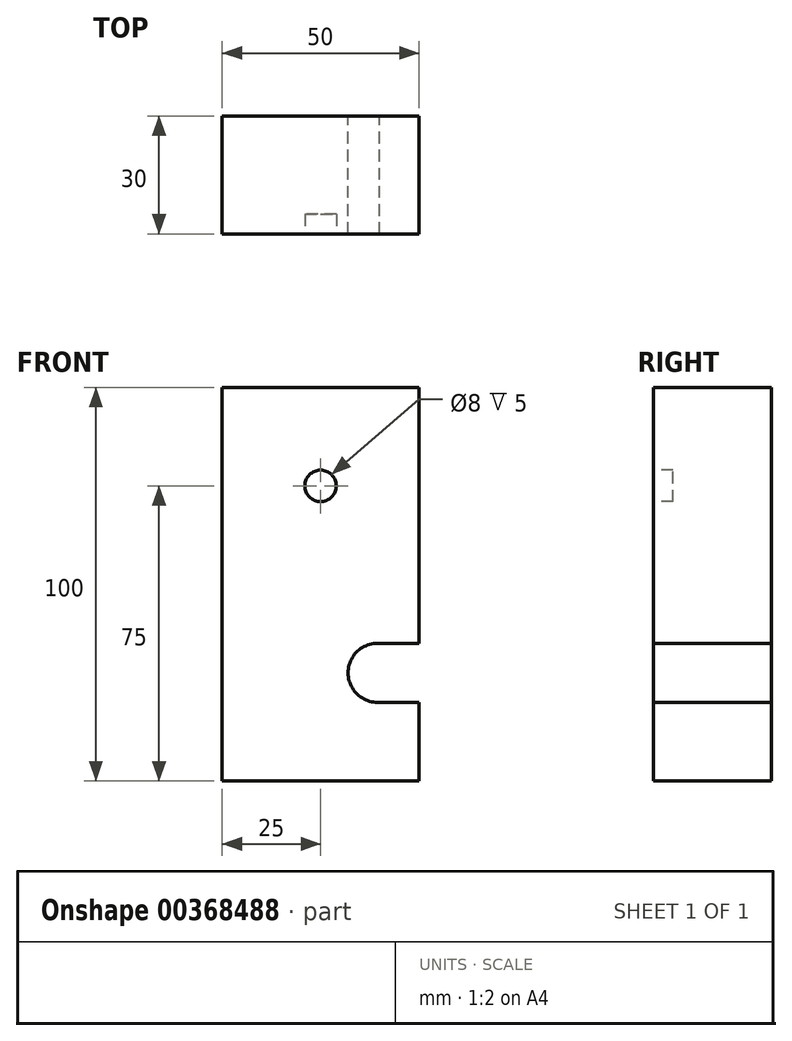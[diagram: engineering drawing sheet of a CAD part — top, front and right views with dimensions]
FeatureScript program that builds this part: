
annotation { "Feature Type Name" : "Feature", "Feature Type Description" : "" }
export const myFeature = defineFeature(function(context is Context, id is Id, definition is map)
    precondition{}
    {
        {
            var Q0;
            Q0=qCreatedBy(makeId("Front.planeOp"),FACE);
            var sketch = newSketch(context, id + "F0", { "sketchPlane" : qUnion([Q0])});
            skLineSegment(sketch, "E0.bottom", {"start": v(-50, 50) * mm, "end": v(0, 50) * mm});
            skLineSegment(sketch, "E0.top", {"start": v(-50, -50) * mm, "end": v(0, -50) * mm});
            skLineSegment(sketch, "E0.left", {"start": v(-50, 50) * mm, "end": v(-50, -50) * mm});
            skPoint(sketch, "E0.middle", {"position": v(0, 0) * mm});
            skLineSegment(sketch, "E1", {"start": v(0, 50) * mm, "end": v(0, -15) * mm});
            skPoint(sketch, "E0.right.start.orphan", {"position": v(50, 50) * mm});
            skPoint(sketch, "E2.orphan", {"position": v(50, -50) * mm});
            skLineSegment(sketch, "E3.bottom", {"start": v(0, -15) * mm, "end": v(-10, -15) * mm});
            skLineSegment(sketch, "E3.top", {"start": v(0, -30) * mm, "end": v(-10, -30) * mm});
            skArc(sketch, "E4", {"start": v(-10, -15) * mm, "mid": v(-18, -22.5) * mm, "end": v(-10, -30) * mm});
            skLineSegment(sketch, "E5.trimOffspring", {"start": v(0, -30) * mm, "end": v(0, -50) * mm});
            skSolve(sketch);
        }
        {
            var Q0;
            Q0 = qSketchRegion(id + "F0", true);
            extrude(context, id + "F1", {"entities" : qUnion([Q0]), "endBound" : BoundingType.SYMMETRIC, "depth" : 30 * mm});
        }
        {
            var Q0;
            Q0=makeQuery(id+"F1.opExtrude","CAP_FACE",FACE,{"disambiguationData":[OSD([sQuery(id+"F0.wireOp",EDGE,"E0.bottom"),sQuery(id+"F0.wireOp",EDGE,"E0.top"),sQuery(id+"F0.wireOp",EDGE,"E0.left"),sQuery(id+"F0.wireOp",EDGE,"E1"),sQuery(id+"F0.wireOp",EDGE,"E3.bottom"),sQuery(id+"F0.wireOp",EDGE,"E3.top"),sQuery(id+"F0.wireOp",EDGE,"E4"),sQuery(id+"F0.wireOp",EDGE,"E5.trimOffspring")])],"isStart":false});
            var sketch = newSketch(context, id + "F2", { "sketchPlane" : qUnion([Q0])});
            skCircle(sketch, "E6", {"center": v(-25, 25) * mm, "radius": 4 * mm});
            skSolve(sketch);
        }
        {
            var Q0;
            Q0 = qSketchRegion(id + "F2", true);
            extrude(context, id + "F3", {"entities" : qUnion([Q0]), "operationType" : NewBodyOperationType.REMOVE, "oppositeDirection" : true, "depth" : 5 * mm});
        }
    });
